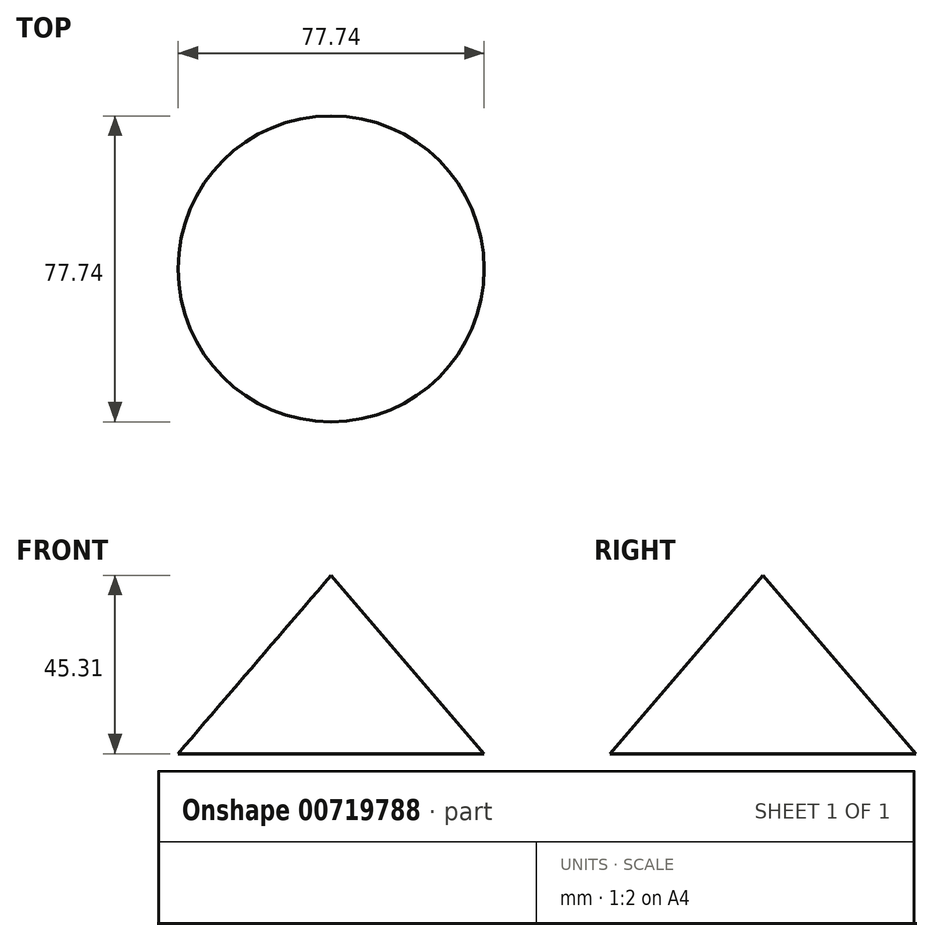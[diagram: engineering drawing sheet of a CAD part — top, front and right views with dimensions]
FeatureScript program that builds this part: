
annotation { "Feature Type Name" : "Feature", "Feature Type Description" : "" }
export const myFeature = defineFeature(function(context is Context, id is Id, definition is map)
    precondition{}
    {
        {
            var Q0;
            Q0=qCreatedBy(makeId("Front.planeOp"),FACE);
            var sketch = newSketch(context, id + "F0", { "sketchPlane" : qUnion([Q0])});
            skLineSegment(sketch, "E0", {"start": v(-38.87, 0) * mm, "end": v(0, 0) * mm});
            skLineSegment(sketch, "E1", {"start": v(0, 0) * mm, "end": v(0, 45.3) * mm});
            skLineSegment(sketch, "E2", {"start": v(0, 45.3) * mm, "end": v(-38.87, 0) * mm});
            skSolve(sketch);
        }
        {
            var Q0;
            Q0=makeQuery(id+"F0.imprint","IMPRINT",FACE,{"disambiguationData":[TD([[makeQuery(id+"F0.imprint","IMPRINT",EDGE,{"derivedFrom":sQuery(id+"F0.wireOp",EDGE,"E0")}),1.0]])]});
            var Q1;
            Q1=sQuery(id+"F0.wireOp",EDGE,"E1");
            revolve(context, id + "F1", {"surfaceOperationType" : NewSurfaceOperationType.NEW, "entities" : qUnion([Q0]), "axis" : qUnion([Q1]), "revolveType" : RevolveType.FULL});
        }
        {
            var Q0;
            Q0=qCreatedBy(makeId("Top.planeOp"),FACE);
            var sketch = newSketch(context, id + "F2", { "sketchPlane" : qUnion([Q0])});
            skLineSegment(sketch, "E3", {"start": v(-16.5, 59.27) * mm, "end": v(-16.5, -65.17) * mm});
            skSolve(sketch);
        }
        {
            var Q0;
            Q0=sQuery(id+"F2.wireOp",EDGE,"E3");
            extrude(context, id + "F3", {"bodyType" : ToolBodyType.SURFACE, "surfaceEntities" : qUnion([Q0]), "depth" : 70.1 * mm, "offsetDistance" : 25.4 * mm});
        }
    });
